# Revit family: agtatec_Record_FldngDoor_FTA-FBO_CurtainWallPanel_RVT2020
name_source: partatom
category: Doors
units: mm (PartAtom-declared; Revit-internal decimal feet)

## family parameters
Always vertical = Yes
Cut with Voids When Loaded = No
OmniClass Number = 23.25.20.14.11.11.17
OmniClass Title = Infill Panels
Room Calculation Point = No
Shared = No

## types (2) — shared parameters
AccessoryOptions = contact manufacturer
AlternativeDoorsetGlazing = part of glazing spec
AntiFingerTrapRequirement = Yes
AssetType = fixed
Category = folding door
CodePerformance = EN16005, EN16361, etc.
Color = customer specific
Configuration = 2-leaf folding door
DoorFrameWidth = 1500 mm
DoorIncluded = Yes
DoorSeal = Yes
DoorsetFasteners = screws
DoorsetOperation = automatic
Double = Yes
DurationUnit = year
ElectronicLock = Yes
ExpectedLife = 10-15
Features = for escape and emergency routes
Finish = Powder coated, Anodized, customer specific
FrameFinishOptions = Powder coated, Anodized, customer specific
FrameMaterial = <By Category>
FrameProfile = aluminium
FrontDriverProfile = Yes
GlassLayers = 2
GlassThickness1 = 6 mm
GlassThickness2 = 6 mm
GlassType = double glazing
HandicapAccessible = Yes
HasDrive = Yes
IsExternal = Yes
LeafColourOptions = all RAL, customer specific
Manufacturer = record door automation
ManufacturerURL = http://www.record.group
Material = aluminium
ModelReference = depends on the configuration
NBSDescription = folding door
Name = record System 20 FBO
NominalHeight = 0 mm
NominalLength = 0 mm
NominalWidth = 0 mm
OffsetFromWallCenter = 0 mm
OpenDoor = No
OpeningLines = Yes
PanelFrames = agtatec_Record_Sliding Door, Aluminium
PanelGlass = agtatec_Record_Sliding Door, Laminated Safety Glass (Clear)
PanelHeight = 2200 mm
PassageWidthOptions = contact manufacturer
ReplacementCost = depends on the configuration and door type
RestrictedOffsetFromWallCenter = 250 mm
SafetyDevices = contact manufacturer
SelfClosing = Yes
Shape = rectangular
Single = No
SmokeStop = No
ThresholdRequired = Yes
ThresholdStripping = Yes
Uniclass2015Title = Folding doorset
VerticalProfileTypeA = Yes
VerticalProfileTypeB = Yes
WarrantyDescription = Local door manufacturer
WarrantyDurationParts = Local door manufacturer
WarrantyGuarantorParts = Local door manufacturer
Weight = depends on configuration and size
version = 1
zero-valued in all types: Infiltration, ThermalTransmittance

## per-type parameters (varying)
| type | Emergency | VerticalProfileTypeC |
| FBO | Yes | Yes |
| FTA | No | No |

## geometry (parser evidence)
native form markers: Sweep x4
no freeform markers — native parametric forms only
